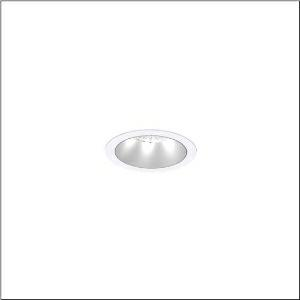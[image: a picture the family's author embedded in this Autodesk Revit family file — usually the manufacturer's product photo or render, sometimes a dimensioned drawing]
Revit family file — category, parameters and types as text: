
# Revit family: lunis_21_m_51db19tc91c
name_source: partatom
category: Lighting Fixtures
units: mm (PartAtom-declared; Revit-internal decimal feet)

## family parameters
Cut with Voids When Loaded = No
Host = Face
Light Source = No
Part Type = Normal
Room Calculation Point = No
Round Connector Dimension = Use Diameter
Shared = No

## types (1)
- --- (1 x LED 3000 K ... 6500 K, 3750 lm, 26 W, 4000K)
    Apparent Load = 26 VA
    CIE Flux Codes = 93 99 100 100 100
    Color Rendering = 80
    Color Temperature = 4000K
    Default Elevation = 1800 mm
    Description = Lunis 21,  M, downlight, light control with lens, of PMMA, anti glare with reflector, of aluminium, matt, light emission: direct distribution, LED rated luminous flux: 3.750lm, light colour: 8tw, with terminal, 5-pole, mains connection: 220..240V, AC/DC, 0/50..60Hz, housing, round, of diecast aluminium, traffic white (RAL 9016), diameter: 115mm, clamping range: 1..40mm, protection rating (complete): IP20, protection rating (on room side): IP54, insulation class (complete): insulation class II (safety insulation), certification: CE, impact resistance: IK03, packaging unit: 1 piece
    Height = 0 mm  [stored 0 ft]
    Lamp = 1 x LED 3000 K ... 6500 K
    Lamp Light Flux = 3750 lm
    Lamp Power = 26 W
    Lamp count = 1
    Length = 115 mm
    Luminous efficacy = 144 lm/W
    Manufacturer = Siteco
    ModVariant = No
    Model = 51DB19TC91C
    Mounting Place = Ceiling
    Mounting Type = Recessed
    Number of Poles = 1
    OnlyDefault = Yes
    Power Factor = 1
    Product Name = Lunis 21 M
    Product group = downlight
    ProductGroupID = 400
    Protection Class = Protection class II
    Protection Degree = IP 20
    RLX_Detail_Level = 1
    RLX_Emergency_Light_Flux = 0 lm
    RLX_Emergency_Type = 0
    RLX_Emergency_Type_DB = No
    RlxData = <blob elided: 11373 chars, md5=af0b341e>
    Socket = socket
    Standby Power = 0 W
    System Light Flux = 3750 lm
    System Power = 26 W
    Type Comments = individual setting: CCT=4000K, colour temperature 4000K, luminous flux: 100 % | (ON | ON | OFF | OFF) | 700 mA
    Type Image = l_1290856.jpg
    URL = http://relux.com
    VarID = @adj_018996
    Voltage = 0 V
    Weight = 0.00 kg
    Width = 0 mm  [stored 0 ft]

note: [stored X ft] marks values corroborated as IEEE doubles in the binary element streams (Revit-internal decimal feet)

## geometry (parser evidence)
native form markers: Sweep x8
no freeform markers — native parametric forms only
